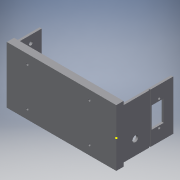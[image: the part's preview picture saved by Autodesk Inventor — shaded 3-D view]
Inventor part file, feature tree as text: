
AUTODESK INVENTOR PART (.ipt)
format: ipt  version: 2018 (Build 220112000, 112)  size: 231,936 bytes
history: native  units: mm
features: extrude x9, sketch x9
ambient origin geometry x8: Origin, YZ Plane, XZ Plane, XY Plane, X Axis, Y Axis, Z Axis, Center Point
bodies: Solid1 (feature_tree)
feature tree (18):
  extrude  "Extrusion1"  Depth=78.0mm
  extrude  "Extrusion4"  Depth=5.0mm
  extrude  "Extrusion5"  Depth=5.0mm
  sketch  "Sketch6"  dims[d17=35.0mm d18=150.0mm d19=0.0mm]
  extrude  "Extrusion8"  Depth=150.0mm TaperAngle=0.0deg
  extrude  "Extrusion9"  Depth=72.0mm
  extrude  "Extrusion10"  Depth=42.0mm
  sketch  "Sketch11"  dims[d36=7.1mm d37=4.05mm]
  extrude  "Extrusion12"  Depth=20.0mm
  extrude  "Extrusion13"  Depth=4.05mm
  extrude  "Extrusion14"  Depth=10.0mm
  sketch  "Sketch1"  dims[d0=150.0mm d1=78.0mm]
  sketch  "Sketch4"  dims[d2=45.0mm d3=0.0mm d14=5.0mm]
  sketch  "Sketch5"  dims[d15=35.0mm d16=5.0mm]
  sketch  "Sketch8"  dims[d20=144.0mm d21=72.0mm]
  sketch  "Sketch9"  dims[d22=42.0mm d23=0.0mm d25=8.0mm]
  sketch  "Sketch10"  dims[d33=20.0mm d34=8.1mm]
  sketch  "Sketch12"  dims[d42=85.0mm d43=53.0mm d44=3.2mm d45=3.2mm d46=3.2mm d47=3.2mm d48=3.0mm d49=0.0mm d51=25.0mm d52=33.0mm d53=0.0mm d54=29.0mm d55=16.5mm d56=45.0mm d59=13.0mm d60=34.0mm d61=3.2mm d62=5.0mm d63=3.0mm d64=0.0mm d67=21.5mm d68=20.0mm d69=45.0mm d70=2.0mm d71=1.0mm d72=0.0mm d74=10.5mm d75=9.4mm d77=30.0mm d81=13.6mm d83=10.0mm d84=0.0mm d85=9.4mm d86=4.15mm d87=15.0mm d88=5.0mm d89=13.6mm d90=7.1mm d91=4.05mm d92=9.4mm d93=4.15mm d94=15.0mm d95=5.0mm d96=17.0mm d97=13.6mm d98=10.0mm d99=0.0mm]
